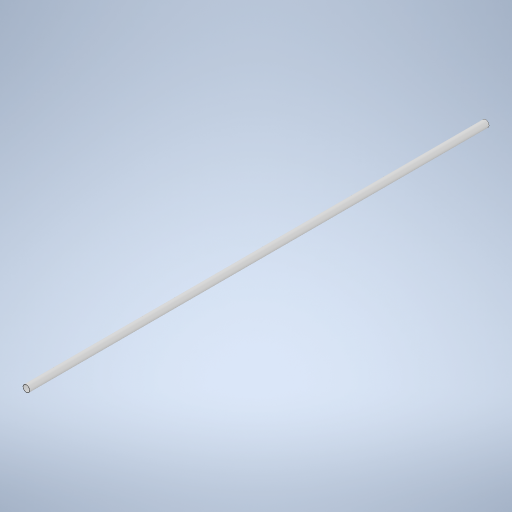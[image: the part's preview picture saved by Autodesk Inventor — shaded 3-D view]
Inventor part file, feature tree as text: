
AUTODESK INVENTOR PART (.ipt)
format: ipt  version: 2023 (Build 270158000, 158)  size: 237,056 bytes
history: native  units: mm
features: extrude x1, sketch x1
ambient origin geometry x8: Origin, YZ Plane, XZ Plane, XY Plane, X Axis, Y Axis, Z Axis, Center Point
bodies: Solido1 (feature_tree)
feature tree (2):
  extrude  "Estrusione1"  Depth=88.9mm
  sketch  "Schizzo1"
